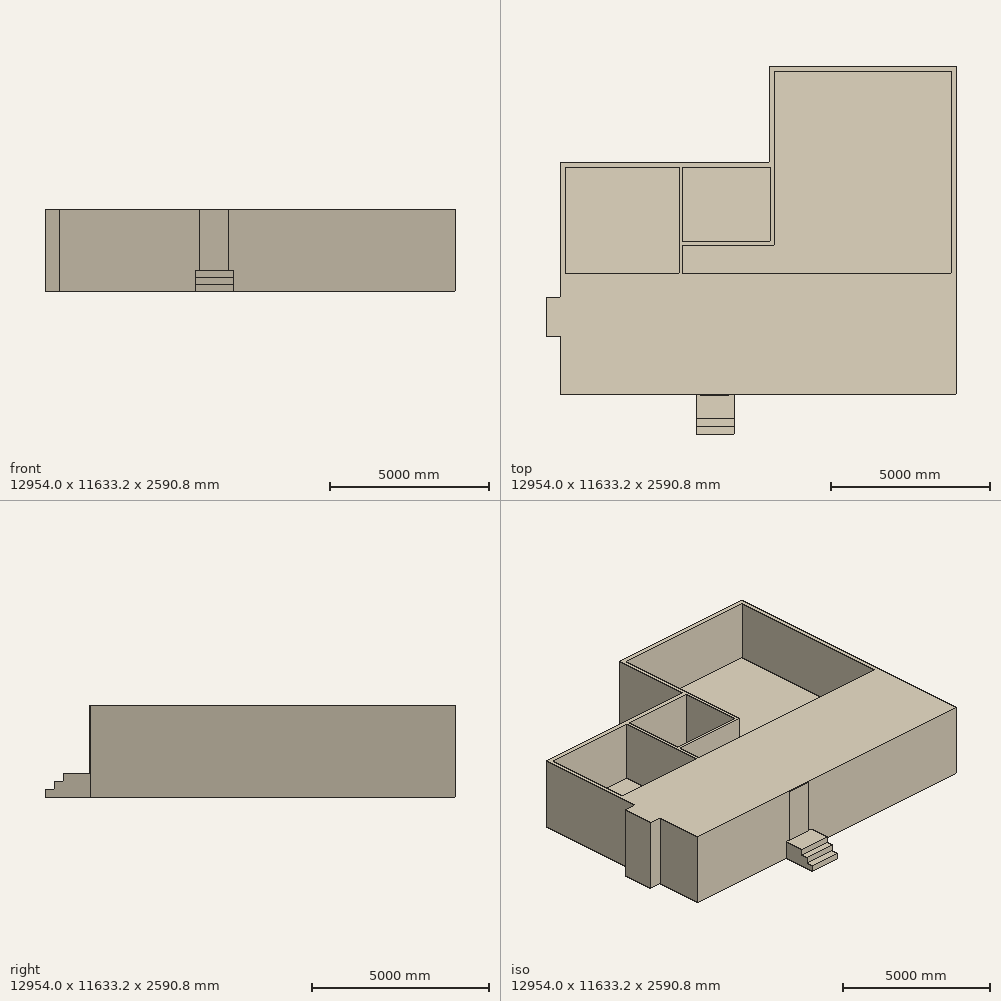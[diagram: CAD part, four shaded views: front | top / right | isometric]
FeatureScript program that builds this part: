
annotation { "Feature Type Name" : "Feature", "Feature Type Description" : "" }
export const myFeature = defineFeature(function(context is Context, id is Id, definition is map)
    precondition{}
    {
        {
            var Q0;
            Q0=qCreatedBy(makeId("Right.planeOp"),FACE);
            var sketch = newSketch(context, id + "F0", { "sketchPlane" : qUnion([Q0])});
            skLineSegment(sketch, "E0", {"start": v(-3657.6, 0) * mm, "end": v(3657.6, 0) * mm});
            skLineSegment(sketch, "E1", {"start": v(3657.6, 0) * mm, "end": v(3657.6, 5080) * mm});
            skLineSegment(sketch, "E2", {"start": v(3657.6, 5080) * mm, "end": v(0, 5842) * mm});
            skLineSegment(sketch, "E3", {"start": v(0, 5842) * mm, "end": v(-3657.6, 2540) * mm});
            skLineSegment(sketch, "E4", {"start": v(-3657.6, 2540) * mm, "end": v(-3657.6, 0) * mm});
            skSolve(sketch);
        }
        {
            var Q0;
            Q0=makeQuery(id+"F0.imprint","IMPRINT",FACE,{"disambiguationData":[TD([[makeQuery(id+"F0.imprint","IMPRINT",EDGE,{"derivedFrom":sQuery(id+"F0.wireOp",EDGE,"E0")}),1.0]])]});
            extrude(context, id + "F1", {"entities" : qUnion([Q0]), "depth" : 9753.6 * mm, "symmetric" : true});
        }
        {
            var Q0;
            Q0=makeQuery(id+"F1.opExtrude","CAP_FACE",FACE,{"disambiguationData":[OSD([sQuery(id+"F0.wireOp",EDGE,"E0"),sQuery(id+"F0.wireOp",EDGE,"E1"),sQuery(id+"F0.wireOp",EDGE,"E2"),sQuery(id+"F0.wireOp",EDGE,"E3"),sQuery(id+"F0.wireOp",EDGE,"E4")])],"isStart":true});
            var sketch = newSketch(context, id + "F2", { "sketchPlane" : qUnion([Q0])});
            skLineSegment(sketch, "E5.0", {"start": v(-3657.6, 5080) * mm, "end": v(0, 5842) * mm});
            skLineSegment(sketch, "E6.0", {"start": v(-3657.6, 2540) * mm, "end": v(-3657.6, 5080) * mm});
            skLineSegment(sketch, "E7", {"start": v(0, 5842) * mm, "end": v(0, 0) * mm, "construction": true});
            skLineSegment(sketch, "E8", {"start": v(0, 5842) * mm, "end": v(-3657.6, 2540) * mm});
            skPoint(sketch, "E9.orphan", {"position": v(-3657.6, 0) * mm});
            skSolve(sketch);
        }
        {
            var Q0;
            Q0=makeQuery(id+"F2.imprint","IMPRINT",FACE,{"disambiguationData":[TD([[makeQuery(id+"F2.imprint","IMPRINT",EDGE,{"derivedFrom":sQuery(id+"F2.wireOp",EDGE,"E5.0")}),-1.0]])]});
            extrude(context, id + "F3", {"entities" : qUnion([Q0]), "operationType" : NewBodyOperationType.REMOVE, "oppositeDirection" : true, "depth" : 457.2 * mm});
        }
        {
            var Q0;
            Q0=makeQuery(id+"F1.opExtrude","CAP_FACE",FACE,{"disambiguationData":[OSD([sQuery(id+"F0.wireOp",EDGE,"E0"),sQuery(id+"F0.wireOp",EDGE,"E1"),sQuery(id+"F0.wireOp",EDGE,"E2"),sQuery(id+"F0.wireOp",EDGE,"E3"),sQuery(id+"F0.wireOp",EDGE,"E4")])],"isStart":false});
            var sketch = newSketch(context, id + "F4", { "sketchPlane" : qUnion([Q0])});
            skLineSegment(sketch, "E10.0", {"start": v(3657.6, 5080) * mm, "end": v(0, 5842) * mm});
            skLineSegment(sketch, "E11.0", {"start": v(3657.6, 2540) * mm, "end": v(3657.6, 5080) * mm});
            skLineSegment(sketch, "E12.0", {"start": v(0, 5842) * mm, "end": v(3657.6, 2540) * mm});
            skPoint(sketch, "E13.orphan", {"position": v(3657.6, 0) * mm});
            skSolve(sketch);
        }
        {
            var Q0;
            Q0 = qSketchRegion(id + "F4", true);
            extrude(context, id + "F5", {"entities" : qUnion([Q0]), "operationType" : NewBodyOperationType.REMOVE, "oppositeDirection" : true, "depth" : 457.2 * mm});
        }
        {
            var Q0;
            Q0=makeQuery(id+"F1.opExtrude","CAP_FACE",FACE,{"disambiguationData":[OSD([sQuery(id+"F0.wireOp",EDGE,"E0"),sQuery(id+"F0.wireOp",EDGE,"E1"),sQuery(id+"F0.wireOp",EDGE,"E2"),sQuery(id+"F0.wireOp",EDGE,"E3"),sQuery(id+"F0.wireOp",EDGE,"E4")])],"isStart":true});
            var sketch = newSketch(context, id + "F6", { "sketchPlane" : qUnion([Q0])});
            skLineSegment(sketch, "E14.0", {"start": v(1828.8, 0) * mm, "end": v(609.6, 0) * mm});
            skLineSegment(sketch, "E15", {"start": v(609.6, 0) * mm, "end": v(609.6, 7010.4) * mm});
            skLineSegment(sketch, "E16", {"start": v(609.6, 7010.4) * mm, "end": v(1371.6, 7010.4) * mm});
            skLineSegment(sketch, "E17", {"start": v(1371.6, 7010.4) * mm, "end": v(1371.6, 3657.6) * mm});
            skLineSegment(sketch, "E18", {"start": v(1371.6, 3657.6) * mm, "end": v(1828.8, 3048) * mm});
            skLineSegment(sketch, "E19", {"start": v(1828.8, 3048) * mm, "end": v(1828.8, 0) * mm});
            skPoint(sketch, "E20.orphan", {"position": v(3657.6, 0) * mm});
            skPoint(sketch, "E21.orphan", {"position": v(-3657.6, 0) * mm});
            skSolve(sketch);
        }
        {
            var Q0;
            Q0 = qSketchRegion(id + "F6", true);
            extrude(context, id + "F7", {"entities" : qUnion([Q0]), "depth" : 457.2 * mm});
        }
        {
            var Q0;
            Q0=makeQuery(id+"F1.opExtrude","CAP_FACE",FACE,{"disambiguationData":[OSD([sQuery(id+"F0.wireOp",EDGE,"E0"),sQuery(id+"F0.wireOp",EDGE,"E1"),sQuery(id+"F0.wireOp",EDGE,"E2"),sQuery(id+"F0.wireOp",EDGE,"E3"),sQuery(id+"F0.wireOp",EDGE,"E4")])],"isStart":false});
            var sketch = newSketch(context, id + "F8", { "sketchPlane" : qUnion([Q0])});
            skLineSegment(sketch, "E22.0", {"start": v(0, 5842) * mm, "end": v(-3657.6, 2540) * mm});
            skLineSegment(sketch, "E23", {"start": v(-3657.6, 2540) * mm, "end": v(-3911.6, 2540) * mm});
            skLineSegment(sketch, "E24", {"start": v(-3911.6, 2540) * mm, "end": v(-3911.6, 2584.45) * mm});
            skLineSegment(sketch, "E25", {"start": v(-3911.6, 2584.45) * mm, "end": v(0, 6115.76) * mm});
            skLineSegment(sketch, "E26", {"start": v(0, 6115.76) * mm, "end": v(0, 5842) * mm});
            skSolve(sketch);
        }
        {
            var Q0;
            Q0=makeQuery(id+"F8.imprint","IMPRINT",FACE,{"disambiguationData":[TD([[makeQuery(id+"F8.imprint","IMPRINT",EDGE,{"derivedFrom":sQuery(id+"F8.wireOp",EDGE,"E22.0")}),-1.0]])]});
            var Q1;
            Q1=makeQuery(id+"F1.opExtrude","CAP_FACE",FACE,{"disambiguationData":[OSD([sQuery(id+"F0.wireOp",EDGE,"E0"),sQuery(id+"F0.wireOp",EDGE,"E1"),sQuery(id+"F0.wireOp",EDGE,"E2"),sQuery(id+"F0.wireOp",EDGE,"E3"),sQuery(id+"F0.wireOp",EDGE,"E4")])],"isStart":true});
            extrude(context, id + "F9", {"entities" : qUnion([Q0]), "endBound" : BoundingType.UP_TO_SURFACE, "oppositeDirection" : true, "endBoundEntityFace" : qUnion([Q1]), "depth" : 30.48 * mm});
        }
        {
            var Q0;
            Q0=makeQuery(id+"F5.boolean.opBoolean","COPY",FACE,{"derivedFrom":makeQuery(id+"F5.opExtrude","CAP_FACE",FACE,{"disambiguationData":[OSD([sQuery(id+"F4.wireOp",EDGE,"E10.0"),sQuery(id+"F4.wireOp",EDGE,"E11.0"),sQuery(id+"F4.wireOp",EDGE,"E12.0")])],"isStart":false})});
            var sketch = newSketch(context, id + "F10", { "sketchPlane" : qUnion([Q0])});
            skLineSegment(sketch, "E27.0", {"start": v(3657.6, 5080) * mm, "end": v(0, 5842) * mm});
            skLineSegment(sketch, "E28", {"start": v(0, 5842) * mm, "end": v(0, 6115.76) * mm});
            skLineSegment(sketch, "E29", {"start": v(0, 6115.76) * mm, "end": v(3911.6, 5300.84) * mm});
            skLineSegment(sketch, "E30", {"start": v(3911.6, 5300.84) * mm, "end": v(3911.6, 5080) * mm});
            skLineSegment(sketch, "E31", {"start": v(3911.6, 5080) * mm, "end": v(3657.6, 5080) * mm});
            skSolve(sketch);
        }
        {
            var Q0;
            Q0=makeQuery(id+"F10.imprint","IMPRINT",FACE,{"disambiguationData":[TD([[makeQuery(id+"F10.imprint","IMPRINT",EDGE,{"derivedFrom":sQuery(id+"F10.wireOp",EDGE,"E27.0")}),-1.0]])]});
            var Q1;
            Q1=makeQuery(id+"F3.boolean.opBoolean","COPY",FACE,{"derivedFrom":makeQuery(id+"F3.opExtrude","CAP_FACE",FACE,{"disambiguationData":[OSD([sQuery(id+"F2.wireOp",EDGE,"E5.0"),sQuery(id+"F2.wireOp",EDGE,"E6.0"),sQuery(id+"F2.wireOp",EDGE,"E8")])],"isStart":false})});
            extrude(context, id + "F11", {"entities" : qUnion([Q0]), "operationType" : NewBodyOperationType.ADD, "endBound" : BoundingType.UP_TO_SURFACE, "oppositeDirection" : true, "endBoundEntityFace" : qUnion([Q1]), "depth" : 30.48 * mm});
        }
        {
            var Q0;
            Q0=makeQuery(id+"F1.opExtrude","CAP_FACE",FACE,{"disambiguationData":[OSD([sQuery(id+"F0.wireOp",EDGE,"E0"),sQuery(id+"F0.wireOp",EDGE,"E1"),sQuery(id+"F0.wireOp",EDGE,"E2"),sQuery(id+"F0.wireOp",EDGE,"E3"),sQuery(id+"F0.wireOp",EDGE,"E4")])],"isStart":true});
            var sketch = newSketch(context, id + "F12", { "sketchPlane" : qUnion([Q0])});
            skLineSegment(sketch, "E32.0.0", {"start": v(0, 5842) * mm, "end": v(-3657.6, 2540) * mm});
            skLineSegment(sketch, "E32.0.1", {"start": v(-3657.6, 2540) * mm, "end": v(-3657.6, 0) * mm});
            skLineSegment(sketch, "E32.0.2", {"start": v(-3657.6, 0) * mm, "end": v(3657.6, 0) * mm});
            skLineSegment(sketch, "E32.0.3", {"start": v(3657.6, 0) * mm, "end": v(3657.6, 2540) * mm});
            skLineSegment(sketch, "E32.0.4", {"start": v(3657.6, 2540) * mm, "end": v(0, 5842) * mm});
            skLineSegment(sketch, "E33", {"start": v(0, 5842) * mm, "end": v(0, 6115.76) * mm});
            skLineSegment(sketch, "E34", {"start": v(0, 6115.76) * mm, "end": v(-3911.6, 2584.45) * mm});
            skLineSegment(sketch, "E35", {"start": v(-3911.6, 2584.45) * mm, "end": v(-3911.6, 2540) * mm});
            skLineSegment(sketch, "E36", {"start": v(-3911.6, 2540) * mm, "end": v(-3657.6, 2540) * mm});
            skSolve(sketch);
        }
        {
            var Q0;
            Q0=makeQuery(id+"F12.imprint","IMPRINT",FACE,{"disambiguationData":[TD([[makeQuery(id+"F12.imprint","IMPRINT",EDGE,{"derivedFrom":sQuery(id+"F12.wireOp",EDGE,"E32.0.0")}),-1.0]])]});
            var Q1;
            Q1=makeQuery(id+"F3.boolean.opBoolean","COPY",FACE,{"derivedFrom":makeQuery(id+"F3.opExtrude","CAP_FACE",FACE,{"disambiguationData":[OSD([sQuery(id+"F2.wireOp",EDGE,"E5.0"),sQuery(id+"F2.wireOp",EDGE,"E6.0"),sQuery(id+"F2.wireOp",EDGE,"E8")])],"isStart":false})});
            extrude(context, id + "F13", {"entities" : qUnion([Q0]), "operationType" : NewBodyOperationType.ADD, "endBound" : BoundingType.UP_TO_SURFACE, "oppositeDirection" : true, "endBoundEntityFace" : qUnion([Q1]), "depth" : 30.48 * mm});
        }
        {
            var Q0;
            Q0=makeQuery(id+"F1.opExtrude","SWEPT_FACE",FACE,{"disambiguationData":[OSD([sQuery(id+"F0.wireOp",EDGE,"E0")])]});
            var sketch = newSketch(context, id + "F14", { "sketchPlane" : qUnion([Q0])});
            skLineSegment(sketch, "E37.0.0", {"start": v(-4876.8, 3657.6) * mm, "end": v(-4876.8, 1828.8) * mm});
            skLineSegment(sketch, "E37.0.1", {"start": v(-4876.8, -3657.6) * mm, "end": v(4876.8, -3657.6) * mm});
            skLineSegment(sketch, "E37.0.2", {"start": v(4876.8, -3657.6) * mm, "end": v(4876.8, 3657.6) * mm});
            skLineSegment(sketch, "E37.0.3", {"start": v(4876.8, 3657.6) * mm, "end": v(-4876.8, 3657.6) * mm});
            skLineSegment(sketch, "E38.0.1", {"start": v(-4876.8, 1828.8) * mm, "end": v(-5334, 1828.8) * mm});
            skLineSegment(sketch, "E38.0.2", {"start": v(-5334, 1828.8) * mm, "end": v(-5334, 609.6) * mm});
            skLineSegment(sketch, "E38.0.3", {"start": v(-5334, 609.6) * mm, "end": v(-4876.8, 609.6) * mm});
            skLineSegment(sketch, "E39.trimOffspring", {"start": v(-4876.8, 609.6) * mm, "end": v(-4876.8, -3657.6) * mm});
            skSolve(sketch);
        }
        {
            var Q0;
            Q0 = qSketchRegion(id + "F14", true);
            extrude(context, id + "F15", {"entities" : qUnion([Q0]), "operationType" : NewBodyOperationType.ADD, "depth" : 457.2 * mm});
        }
        {
            var Q0;
            Q0=qCreatedBy(makeId("Right.planeOp"),FACE);
            var sketch = newSketch(context, id + "F16", { "sketchPlane" : qUnion([Q0])});
            skLineSegment(sketch, "E40.0", {"start": v(-3657.6, -457.2) * mm, "end": v(-3657.6, 203.2) * mm});
            skLineSegment(sketch, "E41", {"start": v(-3657.6, 203.2) * mm, "end": v(-4419.6, 203.2) * mm});
            skLineSegment(sketch, "E42", {"start": v(-4419.6, 203.2) * mm, "end": v(-4419.6, -16.26) * mm});
            skLineSegment(sketch, "E43", {"start": v(-4419.6, -16.26) * mm, "end": v(-4673.6, -16.26) * mm});
            skLineSegment(sketch, "E44", {"start": v(-4673.6, -16.26) * mm, "end": v(-4673.6, -235.71) * mm});
            skLineSegment(sketch, "E45", {"start": v(-4673.6, -235.71) * mm, "end": v(-4927.6, -235.71) * mm});
            skLineSegment(sketch, "E46", {"start": v(-4927.6, -235.71) * mm, "end": v(-4927.6, -457.2) * mm});
            skLineSegment(sketch, "E47", {"start": v(-4927.6, -457.2) * mm, "end": v(-3657.6, -457.2) * mm});
            skPoint(sketch, "E48.orphan", {"position": v(-3657.6, 0) * mm});
            skSolve(sketch);
        }
        {
            var Q0;
            Q0=makeQuery(id+"F16.imprint","IMPRINT",FACE,{"disambiguationData":[TD([[makeQuery(id+"F16.imprint","IMPRINT",EDGE,{"derivedFrom":sQuery(id+"F16.wireOp",EDGE,"E40.0")}),1.0]])]});
            extrude(context, id + "F17", {"entities" : qUnion([Q0]), "operationType" : NewBodyOperationType.ADD, "depth" : 1219.2 * mm, "symmetric" : true});
        }
        {
            var Q0;
            Q0=makeQuery(id+"F1.opExtrude","SWEPT_FACE",FACE,{"disambiguationData":[OSD([sQuery(id+"F0.wireOp",EDGE,"E4")])]});
            var sketch = newSketch(context, id + "F18", { "sketchPlane" : qUnion([Q0])});
            skLineSegment(sketch, "E49.bottom", {"start": v(-457.2, 203.2) * mm, "end": v(457.2, 203.2) * mm});
            skLineSegment(sketch, "E49.top", {"start": v(-457.2, 2489.2) * mm, "end": v(457.2, 2489.2) * mm});
            skLineSegment(sketch, "E49.left", {"start": v(-457.2, 203.2) * mm, "end": v(-457.2, 2489.2) * mm});
            skLineSegment(sketch, "E49.right", {"start": v(457.2, 203.2) * mm, "end": v(457.2, 2489.2) * mm});
            skSolve(sketch);
        }
        {
            var Q0;
            Q0 = qSketchRegion(id + "F18", true);
            extrude(context, id + "F19", {"entities" : qUnion([Q0]), "depth" : 30.48 * mm});
        }
        {
            var Q0;
            Q0=makeQuery(id+"F1.opExtrude","SWEPT_FACE",FACE,{"disambiguationData":[OSD([sQuery(id+"F0.wireOp",EDGE,"E4")])]});
            var sketch = newSketch(context, id + "F20", { "sketchPlane" : qUnion([Q0])});
            skLineSegment(sketch, "E50.0", {"start": v(7620, 0) * mm, "end": v(3657.6, 0) * mm});
            skLineSegment(sketch, "E51", {"start": v(7620, 0) * mm, "end": v(7620, 5080) * mm});
            skLineSegment(sketch, "E52", {"start": v(7620, 5080) * mm, "end": v(5638.8, 5905.5) * mm});
            skLineSegment(sketch, "E53", {"start": v(5638.8, 5905.5) * mm, "end": v(3657.6, 5080) * mm});
            skLineSegment(sketch, "E54", {"start": v(3657.6, 5080) * mm, "end": v(3657.6, 0) * mm});
            skPoint(sketch, "E55.orphan", {"position": v(609.6, 0) * mm});
            skPoint(sketch, "E56.orphan", {"position": v(4876.8, 0) * mm});
            skLineSegment(sketch, "E57", {"start": v(5638.8, 0) * mm, "end": v(5638.8, 9037.06) * mm, "construction": true});
            skSolve(sketch);
        }
        {
            var Q0;
            Q0 = qSketchRegion(id + "F20", true);
            extrude(context, id + "F21", {"entities" : qUnion([Q0]), "operationType" : NewBodyOperationType.ADD, "oppositeDirection" : true, "depth" : 10363.2 * mm});
        }
        {
            var Q0;
            Q0=makeQuery(id+"F9.opExtrude","CAP_FACE",FACE,{"disambiguationData":[OSD([sQuery(id+"F8.wireOp",EDGE,"E22.0"),sQuery(id+"F8.wireOp",EDGE,"E23"),sQuery(id+"F8.wireOp",EDGE,"E24"),sQuery(id+"F8.wireOp",EDGE,"E25"),sQuery(id+"F8.wireOp",EDGE,"E26")])],"isStart":true});
            var sketch = newSketch(context, id + "F22", { "sketchPlane" : qUnion([Q0])});
            skLineSegment(sketch, "E58.0.0", {"start": v(-3911.6, 2540) * mm, "end": v(-3657.6, 2540) * mm});
            skLineSegment(sketch, "E58.0.3", {"start": v(-3657.6, 2813.76) * mm, "end": v(-3911.6, 2584.45) * mm});
            skLineSegment(sketch, "E58.0.4", {"start": v(-3911.6, 2584.45) * mm, "end": v(-3911.6, 2540) * mm});
            skLineSegment(sketch, "E59", {"start": v(-3657.6, 2540) * mm, "end": v(-3657.6, 2813.76) * mm});
            skSolve(sketch);
        }
        {
            var Q0;
            Q0 = qSketchRegion(id + "F22", true);
            var Q1;
            Q1=makeQuery(id+"F21.opExtrude","SWEPT_FACE",FACE,{"disambiguationData":[OSD([sQuery(id+"F20.wireOp",EDGE,"E51")])]});
            extrude(context, id + "F23", {"entities" : qUnion([Q0]), "operationType" : NewBodyOperationType.ADD, "endBound" : BoundingType.UP_TO_SURFACE, "endBoundEntityFace" : qUnion([Q1]), "depth" : 30.48 * mm});
        }
        {
            var Q0;
            Q0=makeQuery(id+"F5.boolean.opBoolean","COPY",FACE,{"derivedFrom":makeQuery(id+"F5.opExtrude","CAP_FACE",FACE,{"disambiguationData":[OSD([sQuery(id+"F4.wireOp",EDGE,"E10.0"),sQuery(id+"F4.wireOp",EDGE,"E11.0"),sQuery(id+"F4.wireOp",EDGE,"E12.0")])],"isStart":false})});
            var sketch = newSketch(context, id + "F24", { "sketchPlane" : qUnion([Q0])});
            skLineSegment(sketch, "E60.0", {"start": v(2133.6, 5397.5) * mm, "end": v(0, 5842) * mm});
            skLineSegment(sketch, "E60.1", {"start": v(2133.6, 5397.5) * mm, "end": v(492.37, 5397.5) * mm});
            skLineSegment(sketch, "E60.2", {"start": v(0, 5842) * mm, "end": v(-281.35, 5588) * mm});
            skLineSegment(sketch, "E60.3", {"start": v(281.35, 5588) * mm, "end": v(-281.35, 5588) * mm});
            skLineSegment(sketch, "E60.4", {"start": v(281.35, 5588) * mm, "end": v(492.37, 5397.5) * mm});
            skPoint(sketch, "E61.orphan", {"position": v(-3657.6, 2540) * mm});
            skSolve(sketch);
        }
        {
            var Q0;
            Q0 = qSketchRegion(id + "F24", true);
            var Q1;
            Q1=makeQuery(id+"F21.opExtrude","SWEPT_FACE",FACE,{"disambiguationData":[OSD([sQuery(id+"F20.wireOp",EDGE,"E53")])]});
            extrude(context, id + "F25", {"entities" : qUnion([Q0]), "operationType" : NewBodyOperationType.ADD, "endBound" : BoundingType.UP_TO_SURFACE, "endBoundEntityFace" : qUnion([Q1]), "depth" : 30.48 * mm});
        }
        {
            var Q0;
            Q0=makeQuery(id+"F11.opExtrude","CAP_FACE",FACE,{"disambiguationData":[OSD([sQuery(id+"F10.wireOp",EDGE,"E27.0"),sQuery(id+"F10.wireOp",EDGE,"E28"),sQuery(id+"F10.wireOp",EDGE,"E29"),sQuery(id+"F10.wireOp",EDGE,"E30"),sQuery(id+"F10.wireOp",EDGE,"E31")])],"isStart":true});
            var sketch = newSketch(context, id + "F26", { "sketchPlane" : qUnion([Q0])});
            skLineSegment(sketch, "E62.0", {"start": v(0, 5842) * mm, "end": v(3657.6, 5080) * mm});
            skLineSegment(sketch, "E62.1", {"start": v(0, 6115.76) * mm, "end": v(3911.6, 5300.84) * mm});
            skLineSegment(sketch, "E62.2", {"start": v(3911.6, 5300.84) * mm, "end": v(3911.6, 5080) * mm});
            skLineSegment(sketch, "E62.4", {"start": v(3911.6, 5080) * mm, "end": v(3657.6, 5080) * mm});
            skLineSegment(sketch, "E62.6", {"start": v(0, 5842) * mm, "end": v(-454.88, 5431.34) * mm});
            skLineSegment(sketch, "E63", {"start": v(-727.31, 5459.16) * mm, "end": v(0, 6115.76) * mm});
            skPoint(sketch, "E62.5.start.orphan", {"position": v(-3657.6, 2813.76) * mm});
            skPoint(sketch, "E64.end.orphan", {"position": v(-3657.6, 2540) * mm});
            skLineSegment(sketch, "E65", {"start": v(-727.31, 5459.16) * mm, "end": v(-454.88, 5431.34) * mm});
            skLineSegment(sketch, "E66", {"start": v(3657.6, 5080) * mm, "end": v(3911.6, 5080) * mm});
            skSolve(sketch);
        }
        {
            var Q0;
            Q0 = qSketchRegion(id + "F26", true);
            var Q1;
            {var subQ0=sQuery(id+"F20.wireOp",EDGE,"E53");var subQ1=makeQuery(id+"F21.opExtrude","SWEPT_FACE",FACE,{"disambiguationData":[OSD([subQ0])]});var subQ5=sQuery(id+"F0.wireOp",EDGE,"E4");Q1=makeQuery(id+"F25.boolean.opBoolean","SPLIT",FACE,{"disambiguationData":[TD([makeQuery(id+"F1.opExtrude","SWEPT_FACE",FACE,{"disambiguationData":[OSD([subQ5])]})])],"derivedFrom":subQ1});}
            extrude(context, id + "F27", {"entities" : qUnion([Q0]), "operationType" : NewBodyOperationType.ADD, "endBound" : BoundingType.UP_TO_SURFACE, "endBoundEntityFace" : qUnion([Q1]), "depth" : 30.48 * mm});
        }
        {
            var Q0;
            Q0=makeQuery(id+"F1.opExtrude","SWEPT_FACE",FACE,{"disambiguationData":[OSD([sQuery(id+"F0.wireOp",EDGE,"E1")])]});
            var sketch = newSketch(context, id + "F28", { "sketchPlane" : qUnion([Q0])});
            skLineSegment(sketch, "E67.0.0", {"start": v(-3657.6, 0) * mm, "end": v(-3657.6, 5080) * mm});
            skLineSegment(sketch, "E67.0.1", {"start": v(-1701.8, 4265.08) * mm, "end": v(-3657.6, 5080) * mm});
            skLineSegment(sketch, "E67.0.4", {"start": v(-3657.6, 0) * mm, "end": v(-1701.8, 0) * mm});
            skLineSegment(sketch, "E68", {"start": v(-1701.8, 0) * mm, "end": v(-1701.8, 4265.08) * mm});
            skPoint(sketch, "E69.orphan", {"position": v(-5638.8, 5905.5) * mm});
            skPoint(sketch, "E70.orphan", {"position": v(-7620, 0) * mm});
            skSolve(sketch);
        }
        {
            var Q0;
            Q0 = qSketchRegion(id + "F28", true);
            var Q1;
            Q1=makeQuery(id+"F21.opExtrude","CAP_FACE",FACE,{"disambiguationData":[OSD([sQuery(id+"F20.wireOp",EDGE,"E50.0"),sQuery(id+"F20.wireOp",EDGE,"E51"),sQuery(id+"F20.wireOp",EDGE,"E52"),sQuery(id+"F20.wireOp",EDGE,"E53"),sQuery(id+"F20.wireOp",EDGE,"E54")])],"isStart":false});
            extrude(context, id + "F29", {"entities" : qUnion([Q0]), "operationType" : NewBodyOperationType.ADD, "endBound" : BoundingType.UP_TO_SURFACE, "endBoundEntityFace" : qUnion([Q1]), "depth" : 30.48 * mm});
        }
        {
            var Q0;
            Q0=makeQuery(id+"F29.boolean.opBoolean","MERGE",FACE,{"derivedFrom":[makeQuery(id+"F21.boolean.opBoolean","MERGE",FACE,{"derivedFrom":[makeQuery(id+"F1.opExtrude","SWEPT_FACE",FACE,{"disambiguationData":[OSD([sQuery(id+"F0.wireOp",EDGE,"E0")])]}),makeQuery(id+"F21.opExtrude","SWEPT_FACE",FACE,{"disambiguationData":[OSD([sQuery(id+"F20.wireOp",EDGE,"E50.0")])]})]}),makeQuery(id+"F29.opExtrude","SWEPT_FACE",FACE,{"disambiguationData":[OSD([sQuery(id+"F28.wireOp",EDGE,"E67.0.4")])]})]});
            var sketch = newSketch(context, id + "F30", { "sketchPlane" : qUnion([Q0])});
            skLineSegment(sketch, "E71", {"start": v(7620, 3657.6) * mm, "end": v(7620, -6705.6) * mm});
            skLineSegment(sketch, "E72", {"start": v(7620, -6705.6) * mm, "end": v(1701.8, -6705.6) * mm});
            skLineSegment(sketch, "E73", {"start": v(1701.8, -6705.6) * mm, "end": v(1701.8, -3657.6) * mm});
            skLineSegment(sketch, "E74", {"start": v(1701.8, -3657.6) * mm, "end": v(4876.8, -3657.6) * mm});
            skLineSegment(sketch, "E75", {"start": v(4876.8, -3657.6) * mm, "end": v(4876.8, 3657.6) * mm});
            skLineSegment(sketch, "E76", {"start": v(4876.8, 3657.6) * mm, "end": v(7620, 3657.6) * mm});
            skSolve(sketch);
        }
        {
            var Q0;
            Q0=makeQuery(id+"F30.imprint","IMPRINT",FACE,{"disambiguationData":[TD([[makeQuery(id+"F30.imprint","IMPRINT",EDGE,{"derivedFrom":sQuery(id+"F30.wireOp",EDGE,"E71")}),1.0]])]});
            var Q1;
            Q1=makeQuery(id+"F17.boolean.opBoolean","MERGE",FACE,{"derivedFrom":[makeQuery(id+"F15.opExtrude","CAP_FACE",FACE,{"disambiguationData":[OSD([sQuery(id+"F14.wireOp",EDGE,"E37.0.0"),sQuery(id+"F14.wireOp",EDGE,"E37.0.1"),sQuery(id+"F14.wireOp",EDGE,"E37.0.2"),sQuery(id+"F14.wireOp",EDGE,"E37.0.3"),sQuery(id+"F14.wireOp",EDGE,"E38.0.1"),sQuery(id+"F14.wireOp",EDGE,"E38.0.2"),sQuery(id+"F14.wireOp",EDGE,"E38.0.3"),sQuery(id+"F14.wireOp",EDGE,"E39.trimOffspring")])],"isStart":false}),makeQuery(id+"F17.opExtrude","SWEPT_FACE",FACE,{"disambiguationData":[OSD([sQuery(id+"F16.wireOp",EDGE,"E47")])]})]});
            extrude(context, id + "F31", {"entities" : qUnion([Q0]), "operationType" : NewBodyOperationType.ADD, "endBound" : BoundingType.UP_TO_SURFACE, "endBoundEntityFace" : qUnion([Q1]), "depth" : 30.48 * mm});
        }
        {
            var Q0;
            Q0=makeQuery(id+"F21.boolean.opBoolean","MERGE",FACE,{"derivedFrom":[makeQuery(id+"F1.opExtrude","SWEPT_FACE",FACE,{"disambiguationData":[OSD([sQuery(id+"F0.wireOp",EDGE,"E4")])]}),makeQuery(id+"F21.opExtrude","CAP_FACE",FACE,{"disambiguationData":[OSD([sQuery(id+"F20.wireOp",EDGE,"E50.0"),sQuery(id+"F20.wireOp",EDGE,"E51"),sQuery(id+"F20.wireOp",EDGE,"E52"),sQuery(id+"F20.wireOp",EDGE,"E53"),sQuery(id+"F20.wireOp",EDGE,"E54")])],"isStart":true})]});
            var sketch = newSketch(context, id + "F32", { "sketchPlane" : qUnion([Q0])});
            skLineSegment(sketch, "E77", {"start": v(5638.8, 5905.5) * mm, "end": v(3505.2, 5016.5) * mm});
            skLineSegment(sketch, "E78", {"start": v(3505.2, 5016.5) * mm, "end": v(3505.2, 5236.63) * mm});
            skLineSegment(sketch, "E79", {"start": v(3505.2, 5236.63) * mm, "end": v(5638.8, 6125.63) * mm});
            skLineSegment(sketch, "E80", {"start": v(5638.8, 5905.5) * mm, "end": v(7772.4, 5016.5) * mm});
            skLineSegment(sketch, "E81", {"start": v(7772.4, 5016.5) * mm, "end": v(7772.4, 5236.63) * mm});
            skLineSegment(sketch, "E82", {"start": v(7772.4, 5236.63) * mm, "end": v(5638.8, 6125.63) * mm});
            skSolve(sketch);
        }
        {
            var Q0;
            Q0 = qSketchRegion(id + "F32", true);
            var Q1;
            Q1=makeQuery(id+"F29.boolean.opBoolean","MERGE",FACE,{"derivedFrom":[makeQuery(id+"F21.opExtrude","CAP_FACE",FACE,{"disambiguationData":[OSD([sQuery(id+"F20.wireOp",EDGE,"E50.0"),sQuery(id+"F20.wireOp",EDGE,"E51"),sQuery(id+"F20.wireOp",EDGE,"E52"),sQuery(id+"F20.wireOp",EDGE,"E53"),sQuery(id+"F20.wireOp",EDGE,"E54")])],"isStart":false}),makeQuery(id+"F29.opExtrude","CAP_FACE",FACE,{"disambiguationData":[OSD([sQuery(id+"F28.wireOp",EDGE,"E67.0.0"),sQuery(id+"F28.wireOp",EDGE,"E67.0.1"),sQuery(id+"F28.wireOp",EDGE,"E67.0.4"),sQuery(id+"F28.wireOp",EDGE,"E68")])],"isStart":false})]});
            extrude(context, id + "F33", {"entities" : qUnion([Q0]), "operationType" : NewBodyOperationType.ADD, "endBound" : BoundingType.UP_TO_SURFACE, "oppositeDirection" : true, "endBoundEntityFace" : qUnion([Q1]), "depth" : 6096 * mm});
        }
        {
            var Q0;
            Q0=makeQuery(id+"F29.boolean.opBoolean","MERGE",FACE,{"derivedFrom":[makeQuery(id+"F21.opExtrude","CAP_FACE",FACE,{"disambiguationData":[OSD([sQuery(id+"F20.wireOp",EDGE,"E50.0"),sQuery(id+"F20.wireOp",EDGE,"E51"),sQuery(id+"F20.wireOp",EDGE,"E52"),sQuery(id+"F20.wireOp",EDGE,"E53"),sQuery(id+"F20.wireOp",EDGE,"E54")])],"isStart":false}),makeQuery(id+"F29.opExtrude","CAP_FACE",FACE,{"disambiguationData":[OSD([sQuery(id+"F28.wireOp",EDGE,"E67.0.0"),sQuery(id+"F28.wireOp",EDGE,"E67.0.1"),sQuery(id+"F28.wireOp",EDGE,"E67.0.4"),sQuery(id+"F28.wireOp",EDGE,"E68")])],"isStart":false})]});
            var sketch = newSketch(context, id + "F34", { "sketchPlane" : qUnion([Q0])});
            skPoint(sketch, "E83.orphan", {"position": v(-6426.2, 7689.4) * mm});
            skLineSegment(sketch, "E84.0", {"start": v(-3505.2, 5016.5) * mm, "end": v(-1549.4, 4201.58) * mm});
            skLineSegment(sketch, "E85.0", {"start": v(-3505.2, 5236.63) * mm, "end": v(-3505.2, 5016.5) * mm});
            skLineSegment(sketch, "E86.0", {"start": v(-3505.2, 5236.63) * mm, "end": v(-1549.4, 4421.72) * mm});
            skLineSegment(sketch, "E87", {"start": v(-1549.4, 4201.58) * mm, "end": v(-1549.4, 4421.72) * mm});
            skPoint(sketch, "E88.orphan", {"position": v(-1701.8, 4265.08) * mm});
            skPoint(sketch, "E89.orphan", {"position": v(-5638.8, 6125.63) * mm});
            skPoint(sketch, "E90.orphan", {"position": v(-5638.8, 5905.5) * mm});
            skSolve(sketch);
        }
        {
            var Q0;
            Q0 = qSketchRegion(id + "F34", true);
            var Q1;
            Q1=makeQuery(id+"F1.opExtrude","SWEPT_FACE",FACE,{"disambiguationData":[OSD([sQuery(id+"F0.wireOp",EDGE,"E1")])]});
            var Q2;
            Q2=makeQuery(id+"F1.opExtrude","SWEPT_BODY",BODY,{"disambiguationData":[OSD([sQuery(id+"F0.wireOp",EDGE,"E0"),sQuery(id+"F0.wireOp",EDGE,"E1"),sQuery(id+"F0.wireOp",EDGE,"E2"),sQuery(id+"F0.wireOp",EDGE,"E3"),sQuery(id+"F0.wireOp",EDGE,"E4")])]});
            extrude(context, id + "F35", {"entities" : qUnion([Q0]), "operationType" : NewBodyOperationType.ADD, "endBound" : BoundingType.UP_TO_SURFACE, "oppositeDirection" : true, "endBoundEntityFace" : qUnion([Q1]), "endBoundEntityBody" : qUnion([Q2]), "depth" : 30.48 * mm});
        }
        {
            var Q0;
            Q0=qCreatedBy(makeId("Top.planeOp"),FACE);
            cPlane(context, id + "F36", {"entities" : qUnion([Q0]), "cplaneType" : CPlaneType.OFFSET, "offset" : 2133.6 * mm, "width" : 152.4 * mm, "height" : 152.4 * mm});
        }
        {
            var Q0;
            Q0=qCreatedBy(id+"F36.planeOp",FACE);
            var sketch = newSketch(context, id + "F37", { "sketchPlane" : qUnion([Q0])});
            skLineSegment(sketch, "E91.bottom", {"start": v(-5981.23, 7367.76) * mm, "end": v(8757.7, 7367.76) * mm});
            skLineSegment(sketch, "E91.top", {"start": v(-5981.23, -4998.42) * mm, "end": v(8757.7, -4998.42) * mm});
            skLineSegment(sketch, "E91.left", {"start": v(-5981.23, 7367.76) * mm, "end": v(-5981.23, -4998.42) * mm});
            skLineSegment(sketch, "E91.right", {"start": v(8757.7, 7367.76) * mm, "end": v(8757.7, -4998.42) * mm});
            skSolve(sketch);
        }
        {
            var Q0;
            Q0 = qSketchRegion(id + "F37", true);
            extrude(context, id + "F38", {"entities" : qUnion([Q0]), "operationType" : NewBodyOperationType.REMOVE, "depth" : 6096 * mm});
        }
        {
            var Q0;
            Q0=qCreatedBy(id+"F36.planeOp",FACE);
            var sketch = newSketch(context, id + "F39", { "sketchPlane" : qUnion([Q0])});
            skLineSegment(sketch, "E92.0", {"start": v(-4724.4, 3505.2) * mm, "end": v(-4724.4, 152.4) * mm});
            skLineSegment(sketch, "E92.1", {"start": v(7467.6, 6553.2) * mm, "end": v(7467.6, 152.4) * mm});
            skLineSegment(sketch, "E92.2", {"start": v(7467.6, 6553.2) * mm, "end": v(1854.2, 6553.2) * mm});
            skLineSegment(sketch, "E92.3", {"start": v(-4724.4, -3505.2) * mm, "end": v(7772.4, -3505.2) * mm});
            skLineSegment(sketch, "E92.4", {"start": v(1854.2, 6553.2) * mm, "end": v(1854.2, 3505.2) * mm});
            skLineSegment(sketch, "E93", {"start": v(-4724.4, 38.1) * mm, "end": v(381, 38.1) * mm});
            skLineSegment(sketch, "E94", {"start": v(381, 38.1) * mm, "end": v(381, -2463.8) * mm});
            skLineSegment(sketch, "E95", {"start": v(381, -2463.8) * mm, "end": v(1524, -2463.8) * mm});
            skLineSegment(sketch, "E96", {"start": v(1524, -2463.8) * mm, "end": v(1524, 38.1) * mm});
            skLineSegment(sketch, "E97", {"start": v(1524, 38.1) * mm, "end": v(7467.6, 38.1) * mm});
            skLineSegment(sketch, "E98", {"start": v(1854.2, 3505.2) * mm, "end": v(1854.2, 1054.1) * mm});
            skLineSegment(sketch, "E99", {"start": v(1854.2, 1054.1) * mm, "end": v(-1028.7, 1054.1) * mm});
            skLineSegment(sketch, "E100", {"start": v(-1028.7, 1168.4) * mm, "end": v(1739.9, 1168.4) * mm});
            skLineSegment(sketch, "E101", {"start": v(1739.9, 1168.4) * mm, "end": v(1739.9, 3505.2) * mm});
            skLineSegment(sketch, "E102", {"start": v(-4724.4, 152.4) * mm, "end": v(7467.6, 152.4) * mm});
            skLineSegment(sketch, "E103", {"start": v(-1028.7, 3505.2) * mm, "end": v(-1028.7, 3505.2) * mm});
            skLineSegment(sketch, "E104", {"start": v(-1143, 3505.2) * mm, "end": v(-1143, 152.4) * mm});
            skLineSegment(sketch, "E105", {"start": v(-1143, 3505.2) * mm, "end": v(-4724.4, 3505.2) * mm});
            skLineSegment(sketch, "E106", {"start": v(-1028.7, 3505.2) * mm, "end": v(-1028.7, 1168.4) * mm});
            skLineSegment(sketch, "E107", {"start": v(1739.9, 3505.2) * mm, "end": v(-1028.7, 3505.2) * mm});
            skLineSegment(sketch, "E108", {"start": v(-1028.7, 1054.1) * mm, "end": v(-1028.7, 152.4) * mm});
            skLineSegment(sketch, "E109", {"start": v(-4724.4, 38.1) * mm, "end": v(-4724.4, -3505.2) * mm});
            skLineSegment(sketch, "E110", {"start": v(7772.4, 38.1) * mm, "end": v(7772.4, -3505.2) * mm});
            skSolve(sketch);
        }
        {
            var Q0;
            Q0 = qSketchRegion(id + "F39", true);
            extrude(context, id + "F40", {"entities" : qUnion([Q0]), "operationType" : NewBodyOperationType.REMOVE, "oppositeDirection" : true, "depth" : 2133.6 * mm});
        }
        {
            var Q0;
            Q0=qCreatedBy(makeId("Top.planeOp"),FACE);
            cPlane(context, id + "F41", {"entities" : qUnion([Q0]), "cplaneType" : CPlaneType.OFFSET, "offset" : 5105.4 * mm, "width" : 152.4 * mm, "height" : 152.4 * mm});
        }
        {
            var Q0;
            Q0=qCreatedBy(id+"F41.planeOp",FACE);
            var sketch = newSketch(context, id + "F42", { "sketchPlane" : qUnion([Q0])});
            skLineSegment(sketch, "E111.bottom", {"start": v(-5822.1, 7161.66) * mm, "end": v(8427.56, 7161.66) * mm});
            skLineSegment(sketch, "E111.top", {"start": v(-5822.1, -4497.14) * mm, "end": v(8427.56, -4497.14) * mm});
            skLineSegment(sketch, "E111.left", {"start": v(-5822.1, 7161.66) * mm, "end": v(-5822.1, -4497.14) * mm});
            skLineSegment(sketch, "E111.right", {"start": v(8427.56, 7161.66) * mm, "end": v(8427.56, -4497.14) * mm});
            skSolve(sketch);
        }
        {
            var Q0;
            Q0 = qSketchRegion(id + "F42", true);
            extrude(context, id + "F43", {"entities" : qUnion([Q0]), "operationType" : NewBodyOperationType.REMOVE, "depth" : 3048 * mm});
        }
        {
            var Q0;
            Q0=qCreatedBy(id+"F41.planeOp",FACE);
            var sketch = newSketch(context, id + "F44", { "sketchPlane" : qUnion([Q0])});
            skLineSegment(sketch, "E112.0", {"start": v(-4724.4, 663.53) * mm, "end": v(-4724.4, -1676.4) * mm});
            skLineSegment(sketch, "E112.1", {"start": v(-4267.2, 663.53) * mm, "end": v(-4724.4, 663.53) * mm});
            skLineSegment(sketch, "E112.3", {"start": v(-4267.2, 3505.2) * mm, "end": v(-4267.2, 663.53) * mm});
            skLineSegment(sketch, "E112.6", {"start": v(3129.28, -663.53) * mm, "end": v(3129.28, -3505.2) * mm});
            skLineSegment(sketch, "E112.7", {"start": v(3129.28, -3505.2) * mm, "end": v(7569.2, -3505.2) * mm});
            skLineSegment(sketch, "E112.8", {"start": v(7569.2, -3505.2) * mm, "end": v(7569.2, 6553.2) * mm});
            skLineSegment(sketch, "E112.9", {"start": v(7569.2, 6553.2) * mm, "end": v(1854.2, 6553.2) * mm});
            skLineSegment(sketch, "E113.0", {"start": v(381, 38.1) * mm, "end": v(381, -2463.8) * mm});
            skLineSegment(sketch, "E114.0", {"start": v(1524, -2463.8) * mm, "end": v(1524, 38.1) * mm});
            skLineSegment(sketch, "E115", {"start": v(-4724.4, -1676.4) * mm, "end": v(-457.2, -1676.4) * mm});
            skLineSegment(sketch, "E116", {"start": v(-457.2, -1676.4) * mm, "end": v(-457.2, 3505.2) * mm});
            skLineSegment(sketch, "E117.0", {"start": v(-457.2, 3505.2) * mm, "end": v(-4267.2, 3505.2) * mm});
            skLineSegment(sketch, "E118.0", {"start": v(1739.8, 3505.2) * mm, "end": v(-342.9, 3505.2) * mm});
            skPoint(sketch, "E119.orphan", {"position": v(-4724.4, -289.94) * mm});
            skLineSegment(sketch, "E120", {"start": v(-342.9, 3505.2) * mm, "end": v(-342.9, 1600.2) * mm});
            skLineSegment(sketch, "E121", {"start": v(-342.9, 1600.2) * mm, "end": v(1739.8, 1600.2) * mm});
            skLineSegment(sketch, "E122", {"start": v(1739.8, 1600.2) * mm, "end": v(1739.8, 3505.2) * mm});
            skLineSegment(sketch, "E123.0", {"start": v(1854.2, 6553.2) * mm, "end": v(1854.2, -663.53) * mm});
            skLineSegment(sketch, "E124", {"start": v(3129.28, -663.53) * mm, "end": v(1854.2, -663.53) * mm});
            skPoint(sketch, "E125.orphan", {"position": v(1854.2, -331.01) * mm});
            skLineSegment(sketch, "E126", {"start": v(-342.9, 1485.9) * mm, "end": v(-342.9, 38.1) * mm});
            skLineSegment(sketch, "E127", {"start": v(-342.9, 38.1) * mm, "end": v(381, 38.1) * mm});
            skLineSegment(sketch, "E128", {"start": v(-342.9, 1485.9) * mm, "end": v(1739.8, 1485.9) * mm});
            skLineSegment(sketch, "E129", {"start": v(1739.8, 1485.9) * mm, "end": v(1739.8, 38.1) * mm});
            skLineSegment(sketch, "E130", {"start": v(1739.8, 38.1) * mm, "end": v(1524, 38.1) * mm});
            skLineSegment(sketch, "E131", {"start": v(381, -2463.8) * mm, "end": v(1524, -2463.8) * mm});
            skSolve(sketch);
        }
        {
            var Q0;
            Q0 = qSketchRegion(id + "F44", true);
            extrude(context, id + "F45", {"entities" : qUnion([Q0]), "operationType" : NewBodyOperationType.REMOVE, "oppositeDirection" : true, "depth" : 2286 * mm});
        }
    });
